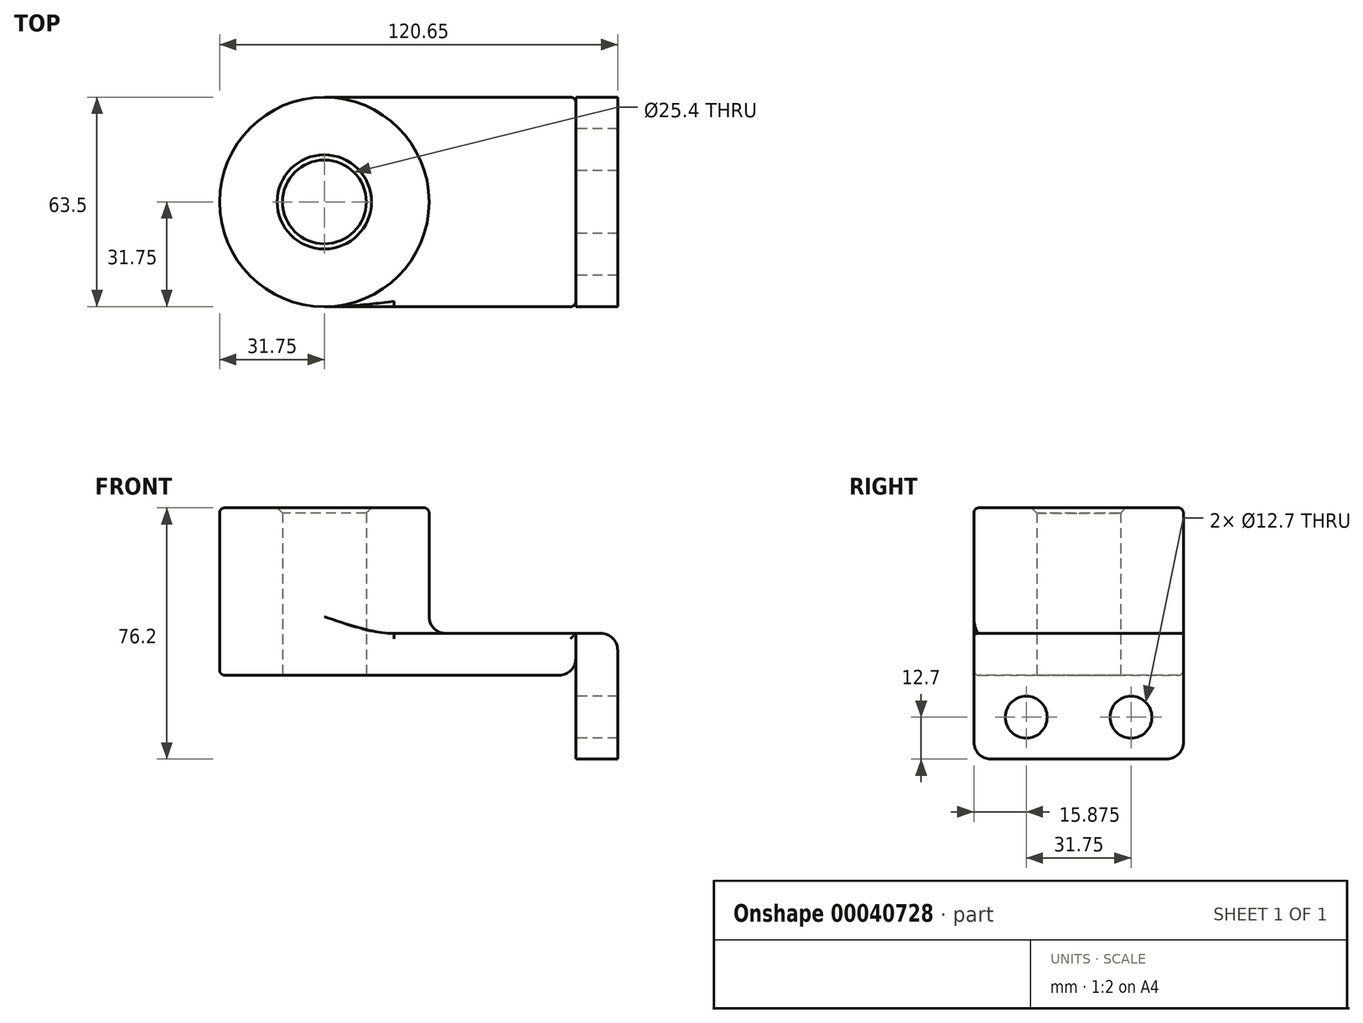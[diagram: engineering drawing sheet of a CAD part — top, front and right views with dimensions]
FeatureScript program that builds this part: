
annotation { "Feature Type Name" : "Feature", "Feature Type Description" : "" }
export const myFeature = defineFeature(function(context is Context, id is Id, definition is map)
    precondition{}
    {
        {
            var Q0;
            Q0=qCreatedBy(makeId("Top.planeOp"),FACE);
            var sketch = newSketch(context, id + "F0", { "sketchPlane" : qUnion([Q0])});
            skLineSegment(sketch, "E0.rect.bottom", {"start": v(38.1, -31.75) * mm, "end": v(-38.1, -31.75) * mm});
            skLineSegment(sketch, "E0.rect.top", {"start": v(38.1, 31.75) * mm, "end": v(-38.1, 31.75) * mm});
            skLineSegment(sketch, "E0.rect.left", {"start": v(38.1, -31.75) * mm, "end": v(38.1, 31.75) * mm});
            skLineSegment(sketch, "E0.rect.right", {"start": v(-38.1, -31.75) * mm, "end": v(-38.1, 31.75) * mm});
            skPoint(sketch, "E0.rect.middle", {"position": v(0, 0) * mm});
            skCircle(sketch, "E1", {"center": v(-38.1, 0) * mm, "radius": 31.75 * mm});
            skCircle(sketch, "E2", {"center": v(-38.1, 0) * mm, "radius": 12.7 * mm});
            skSolve(sketch);
        }
        {
            var Q0;
            {var subQ0=sQuery(id+"F0.wireOp",EDGE,"E2");var subQ1=sQuery(id+"F0.wireOp",EDGE,"E0.rect.right");var subQ3=makeQuery(id+"F0.imprint","INTERSECT",VERTEX,{"disambiguationData":[OD(0.0)],"derivedFrom":[subQ1,subQ0]});Q0=makeQuery(id+"F0.imprint","IMPRINT",FACE,{"disambiguationData":[TD([[makeQuery(id+"F0.imprint","IMPRINT",EDGE,{"disambiguationData":[TD([[subQ3,-1.0]])],"derivedFrom":subQ0}),-1.0]])]});}
            var Q1;
            {var subQ3=sQuery(id+"F0.wireOp",EDGE,"E0.rect.bottom");Q1=makeQuery(id+"F0.imprint","IMPRINT",FACE,{"disambiguationData":[TD([[makeQuery(id+"F0.imprint","IMPRINT",EDGE,{"derivedFrom":subQ3}),-1.0]])]});}
            var Q2;
            {var subQ0=sQuery(id+"F0.wireOp",EDGE,"E2");var subQ1=sQuery(id+"F0.wireOp",EDGE,"E0.rect.right");var subQ3=makeQuery(id+"F0.imprint","INTERSECT",VERTEX,{"disambiguationData":[OD(0.0)],"derivedFrom":[subQ1,subQ0]});Q2=makeQuery(id+"F0.imprint","IMPRINT",FACE,{"disambiguationData":[TD([[makeQuery(id+"F0.imprint","IMPRINT",EDGE,{"disambiguationData":[TD([[subQ3,1.0]])],"derivedFrom":subQ0}),-1.0]])]});}
            extrude(context, id + "F1", {"entities" : qUnion([Q0, Q1, Q2]), "depth" : 12.7 * mm});
        }
        {
            var Q0;
            {var subQ0=sQuery(id+"F0.wireOp",EDGE,"E2");var subQ1=sQuery(id+"F0.wireOp",EDGE,"E0.rect.right");var subQ3=makeQuery(id+"F0.imprint","INTERSECT",VERTEX,{"disambiguationData":[OD(0.0)],"derivedFrom":[subQ1,subQ0]});Q0=makeQuery(id+"F0.imprint","IMPRINT",FACE,{"disambiguationData":[TD([[makeQuery(id+"F0.imprint","IMPRINT",EDGE,{"disambiguationData":[TD([[subQ3,-1.0]])],"derivedFrom":subQ0}),-1.0]])]});}
            var Q1;
            {var subQ0=sQuery(id+"F0.wireOp",EDGE,"E2");var subQ1=sQuery(id+"F0.wireOp",EDGE,"E0.rect.right");var subQ3=makeQuery(id+"F0.imprint","INTERSECT",VERTEX,{"disambiguationData":[OD(0.0)],"derivedFrom":[subQ1,subQ0]});Q1=makeQuery(id+"F0.imprint","IMPRINT",FACE,{"disambiguationData":[TD([[makeQuery(id+"F0.imprint","IMPRINT",EDGE,{"disambiguationData":[TD([[subQ3,1.0]])],"derivedFrom":subQ0}),-1.0]])]});}
            extrude(context, id + "F2", {"entities" : qUnion([Q0, Q1]), "operationType" : NewBodyOperationType.ADD, "depth" : 50.8 * mm});
        }
        {
            var Q0;
            Q0=makeQuery(id+"F1.opExtrude","SWEPT_FACE",FACE,{"disambiguationData":[OSD([sQuery(id+"F0.wireOp",EDGE,"E0.rect.left")])]});
            var sketch = newSketch(context, id + "F3", { "sketchPlane" : qUnion([Q0])});
            skLineSegment(sketch, "E3.bottom", {"start": v(-31.75, 12.7) * mm, "end": v(31.75, 12.7) * mm});
            skLineSegment(sketch, "E3.top", {"start": v(-31.75, -25.4) * mm, "end": v(31.75, -25.4) * mm});
            skLineSegment(sketch, "E3.left", {"start": v(-31.75, 12.7) * mm, "end": v(-31.75, -25.4) * mm});
            skLineSegment(sketch, "E3.right", {"start": v(31.75, 12.7) * mm, "end": v(31.75, -25.4) * mm});
            skLineSegment(sketch, "E4", {"start": v(0, -25.4) * mm, "end": v(0, 0) * mm, "construction": true});
            skCircle(sketch, "E5", {"center": v(-15.88, -12.7) * mm, "radius": 6.35 * mm});
            skCircle(sketch, "E6.MirrorC", {"center": v(79.37, -12.7) * mm, "radius": 6.35 * mm});
            skCircle(sketch, "E7.MirrorC", {"center": v(15.88, -12.7) * mm, "radius": 6.35 * mm});
            skSolve(sketch);
        }
        {
            var Q0;
            {var subQ2=sQuery(id+"F3.wireOp",EDGE,"E3.top");Q0=makeQuery(id+"F3.imprint","IMPRINT",FACE,{"disambiguationData":[TD([[makeQuery(id+"F3.imprint","IMPRINT",EDGE,{"derivedFrom":subQ2}),1.0]])]});}
            var Q1;
            {var subQ1=sQuery(id+"F3.wireOp",EDGE,"E3.bottom");Q1=makeQuery(id+"F3.imprint","IMPRINT",FACE,{"disambiguationData":[TD([[makeQuery(id+"F3.imprint","IMPRINT",EDGE,{"derivedFrom":subQ1}),-1.0]])]});}
            extrude(context, id + "F4", {"entities" : qUnion([Q0, Q1]), "depth" : 12.7 * mm});
        }
        {
            var Q0;
            Q0=makeQuery(id+"F4.opExtrude","CAP_EDGE",EDGE,{"disambiguationData":[OSD([sQuery(id+"F3.wireOp",EDGE,"E3.bottom")])],"isStart":false});
            var Q1;
            Q1=makeQuery(id+"F4.opExtrude","SWEPT_EDGE",EDGE,{"disambiguationData":[OSD([sQuery(id+"F3.wireOp",EDGE,"E3.top"),sQuery(id+"F3.wireOp",EDGE,"E3.left")])]});
            var Q2;
            Q2=makeQuery(id+"F4.opExtrude","SWEPT_EDGE",EDGE,{"disambiguationData":[OSD([sQuery(id+"F3.wireOp",EDGE,"E3.top"),sQuery(id+"F3.wireOp",EDGE,"E3.right")])]});
            var Q3;
            {var subQ0=sQuery(id+"F0.wireOp",EDGE,"E1");Q3=makeQuery(id+"F2.boolean.opBoolean","INTERSECT",EDGE,{"derivedFrom":[makeQuery(id+"F1.opExtrude","CAP_FACE",FACE,{"disambiguationData":[OSD([sQuery(id+"F0.wireOp",EDGE,"E0.rect.bottom"),sQuery(id+"F0.wireOp",EDGE,"E0.rect.top"),sQuery(id+"F0.wireOp",EDGE,"E0.rect.left"),subQ0,sQuery(id+"F0.wireOp",EDGE,"E2")])],"isStart":false}),makeQuery(id+"F2.opExtrude","SWEPT_FACE",FACE,{"disambiguationData":[OSD([subQ0])]})]});}
            var Q4;
            Q4=makeQuery(id+"F1.opExtrude","CAP_EDGE",EDGE,{"disambiguationData":[OSD([sQuery(id+"F0.wireOp",EDGE,"E0.rect.left")])],"isStart":true});
            fillet(context, id + "F5", {"entities" : qUnion([Q0, Q1, Q2, Q3, Q4]), "radius" : 5.08 * mm, "tangentPropagation" : true, "allowEdgeOverflow" : false});
        }
        {
            var Q0;
            Q0=makeQuery(id+"F1.opExtrude","SWEPT_FACE",FACE,{"disambiguationData":[OSD([sQuery(id+"F0.wireOp",EDGE,"E0.rect.bottom")])]});
            var Q1;
            Q1=makeQuery(id+"F2.opExtrude","CAP_EDGE",EDGE,{"disambiguationData":[OSD([sQuery(id+"F0.wireOp",EDGE,"E1")])],"isStart":false});
            fillet(context, id + "F6", {"entities" : qUnion([Q0, Q1]), "radius" : 1.59 * mm, "tangentPropagation" : true, "allowEdgeOverflow" : false});
        }
        {
            var Q0;
            Q0=makeQuery(id+"F2.opExtrude","CAP_EDGE",EDGE,{"disambiguationData":[OSD([sQuery(id+"F0.wireOp",EDGE,"E2")])],"isStart":false});
            chamfer(context, id + "F7", {"entities" : qUnion([Q0]), "width" : 1.59 * mm, "tangentPropagation" : true});
        }
    });
